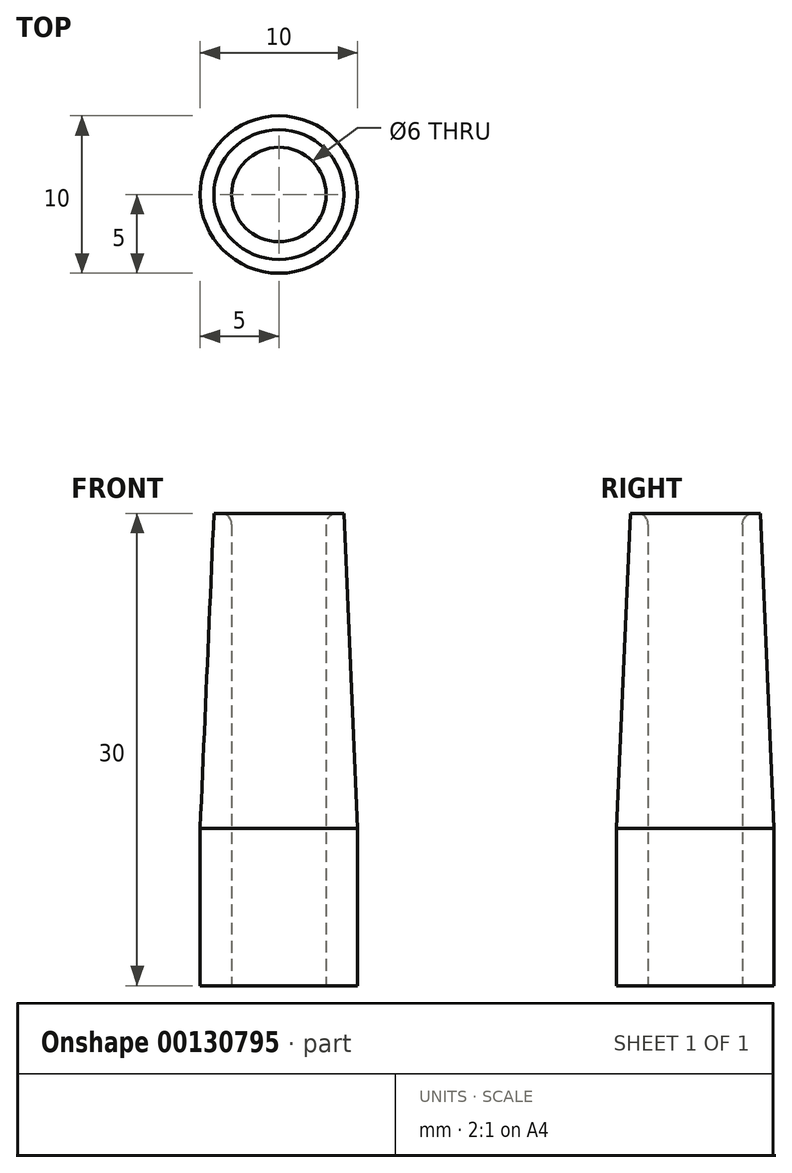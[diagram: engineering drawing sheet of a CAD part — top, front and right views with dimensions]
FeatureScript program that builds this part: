
annotation { "Feature Type Name" : "Feature", "Feature Type Description" : "" }
export const myFeature = defineFeature(function(context is Context, id is Id, definition is map)
    precondition{}
    {
        {
            var Q0;
            Q0=qCreatedBy(makeId("Front.planeOp"),FACE);
            var sketch = newSketch(context, id + "F0", { "sketchPlane" : qUnion([Q0])});
            skLineSegment(sketch, "E0", {"start": v(5, 0) * mm, "end": v(11.85, 0) * mm});
            skLineSegment(sketch, "E1", {"start": v(5, 0) * mm, "end": v(5, 10) * mm});
            skLineSegment(sketch, "E2", {"start": v(5, 10) * mm, "end": v(4.13, 30) * mm});
            skLineSegment(sketch, "E3", {"start": v(4.13, 30) * mm, "end": v(3, 30) * mm});
            skLineSegment(sketch, "E4", {"start": v(3, 30) * mm, "end": v(3, 0) * mm});
            skLineSegment(sketch, "E5", {"start": v(3, 0) * mm, "end": v(11.85, 0) * mm});
            skLineSegment(sketch, "E6", {"start": v(0, -15.77) * mm, "end": v(0, 44.25) * mm, "construction": true});
            skSolve(sketch);
        }
        {
            var Q0;
            Q0 = qSketchRegion(id + "F0", true);
            var Q1;
            Q1=sQuery(id+"F0.wireOp",EDGE,"E6");
            revolve(context, id + "F1", {"entities" : qUnion([Q0]), "axis" : qUnion([Q1]), "revolveType" : RevolveType.FULL});
        }
        {
            var Q0;
            Q0=makeQuery(id+"F1.opRevolve","SWEPT_EDGE",EDGE,{"disambiguationData":[OSD([sQuery(id+"F0.wireOp",EDGE,"E3"),sQuery(id+"F0.wireOp",EDGE,"E4")])]});
            fillet(context, id + "F2", {"entities" : qUnion([Q0]), "radius" : .7 * mm, "tangentPropagation" : true, "allowEdgeOverflow" : false});
        }
    });
